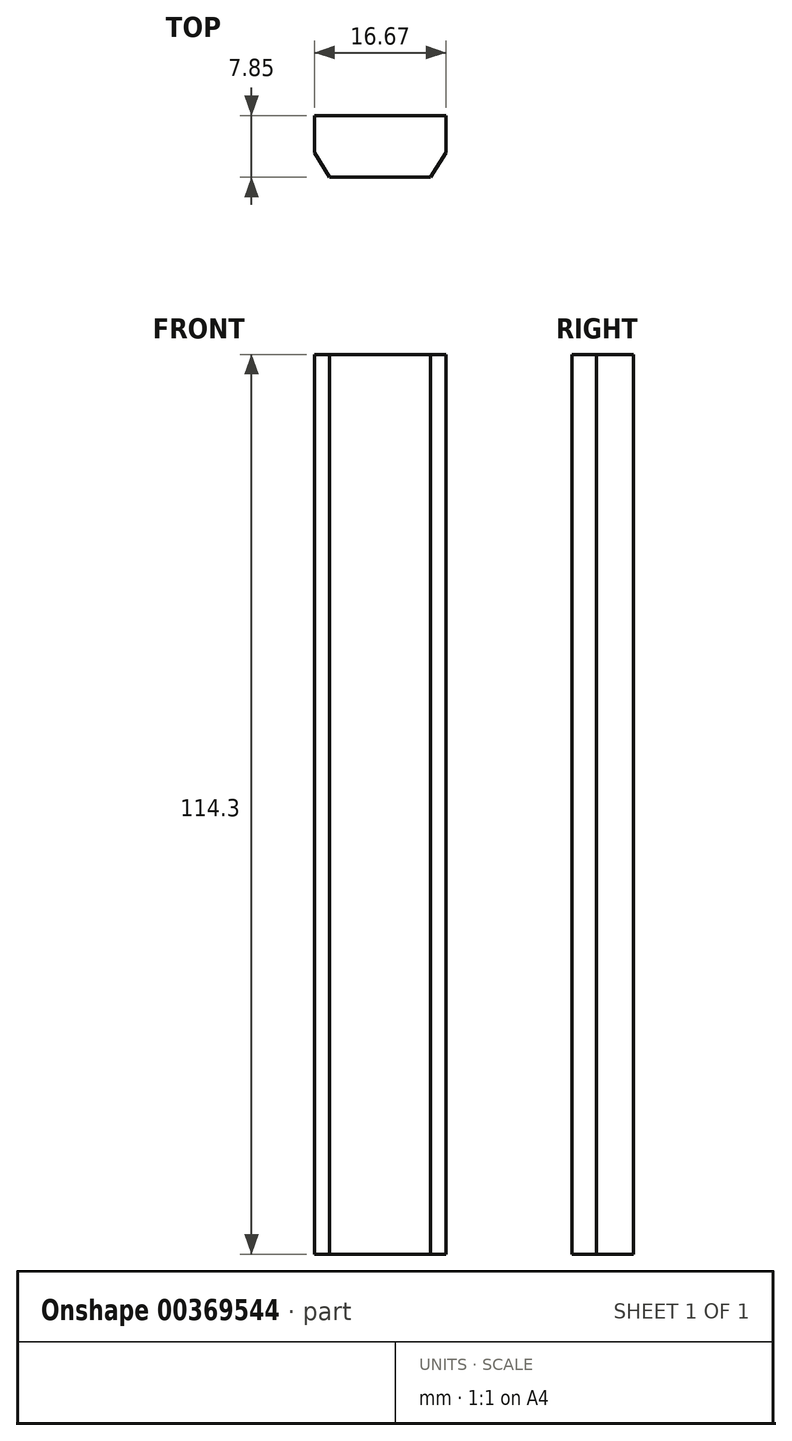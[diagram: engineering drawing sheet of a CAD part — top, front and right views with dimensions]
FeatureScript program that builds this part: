
annotation { "Feature Type Name" : "Feature", "Feature Type Description" : "" }
export const myFeature = defineFeature(function(context is Context, id is Id, definition is map)
    precondition{}
    {
        {
            var Q0;
            Q0=qCreatedBy(makeId("Top.planeOp"),FACE);
            var sketch = newSketch(context, id + "F0", { "sketchPlane" : qUnion([Q0])});
            skLineSegment(sketch, "E0", {"start": v(1.02, 10.56) * mm, "end": v(1.02, 6.16) * mm});
            skLineSegment(sketch, "E1", {"start": v(1.02, 6.16) * mm, "end": v(22.1, 6.16) * mm});
            skLineSegment(sketch, "E2", {"start": v(22.1, 6.16) * mm, "end": v(-19.04, 6.16) * mm});
            skLineSegment(sketch, "E3", {"start": v(14.94, 4.43) * mm, "end": v(9.36, 4.43) * mm});
            skPoint(sketch, "E3.endSnap0", {"position": v(14.94, 4.43) * mm});
            skLineSegment(sketch, "E4", {"start": v(-12.9, 4.43) * mm, "end": v(-7.31, 4.43) * mm});
            skLineSegment(sketch, "E5", {"start": v(-12.9, -1.7) * mm, "end": v(-5.4, -1.7) * mm});
            skLineSegment(sketch, "E6", {"start": v(14.94, -1.7) * mm, "end": v(7.44, -1.7) * mm});
            skLineSegment(sketch, "E7", {"start": v(-7.31, 4.43) * mm, "end": v(-7.31, -5.32) * mm});
            skLineSegment(sketch, "E8", {"start": v(-7.31, -5.32) * mm, "end": v(-7.31, 16.26) * mm});
            skLineSegment(sketch, "E9", {"start": v(9.36, 4.43) * mm, "end": v(9.36, -6.66) * mm});
            skLineSegment(sketch, "E10", {"start": v(9.36, -6.66) * mm, "end": v(9.36, 15.78) * mm});
            skLineSegment(sketch, "E11", {"start": v(-5.4, -1.7) * mm, "end": v(-7.31, 1.43) * mm});
            skLineSegment(sketch, "E12.MirrorCS", {"start": v(7.44, -1.7) * mm, "end": v(9.36, 1.43) * mm});
            skLineSegment(sketch, "E13", {"start": v(-5.4, -1.7) * mm, "end": v(7.44, -1.7) * mm});
            skSolve(sketch);
        }
        {
            var Q0;
            {var subQ5=sQuery(id+"F0.wireOp",EDGE,"E11");Q0=makeQuery(id+"F0.imprint","IMPRINT",FACE,{"disambiguationData":[TD([[makeQuery(id+"F0.imprint","IMPRINT",EDGE,{"derivedFrom":subQ5}),-1.0]])]});}
            extrude(context, id + "F1", {"entities" : qUnion([Q0]), "depth" : 114.3 * mm});
        }
    });
